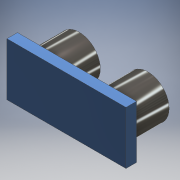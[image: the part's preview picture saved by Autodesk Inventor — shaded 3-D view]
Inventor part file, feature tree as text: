
AUTODESK INVENTOR PART (.ipt)
format: ipt  version: 2016 (Build 200138000, 138)  size: 118,272 bytes
history: native  units: mm
features: extrude x2, sketch x2
ambient origin geometry x8: Origin, YZ Plane, XZ Plane, XY Plane, X Axis, Y Axis, Z Axis, Center Point
bodies: Solid1 (feature_tree)
feature tree (4):
  extrude  "Extrusion1"  Depth=20.0mm
  extrude  "Extrusion2"  Depth=13.8mm
  sketch  "Sketch1"  dims[d0=45.0mm d1=20.0mm]
  sketch  "Sketch2"  dims[d2=4.0mm d3=0.0mm d4=9.5mm d5=9.5mm d6=16.0mm d7=16.0mm d8=26.0mm d9=13.8mm d10=0.0mm]
